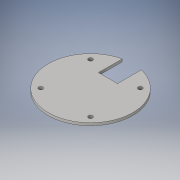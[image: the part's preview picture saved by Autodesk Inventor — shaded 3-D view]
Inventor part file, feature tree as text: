
AUTODESK INVENTOR PART (.ipt)
format: ipt  version: 2016 (Build 200138000, 138)  size: 122,880 bytes
history: native  units: in
note: dims shown in document units (in); Inventor stores cm internally (conversion verified against a paired STEP export)
features: sketch x1, extrude x1, hole x1
ambient origin geometry x8: Origin, YZ Plane, XZ Plane, XY Plane, X Axis, Y Axis, Z Axis, Center Point
bodies: Solid1 (feature_tree)
feature tree (3):
  sketch  "Sketch2"  dims[d1=2.0079in d2=0.4134in d3=0.4528in d4=1.1811in d5=1.1811in d6=0.0625in d7=0.0in d8=0.0984in d9=0.75in d10=0.375in d11=0.25in d12=0.5635in d13=1.0in d14=0.8108in]
  extrude  "Extrusion1"  Depth=0.0625in
  hole  "Hole1"  [1 undecoded]
note: 1 required parameter value undecoded (feature->parameter linkage not recoverable at this tier; creation-order binding heuristic only, values carry confidence <= 0.55)
